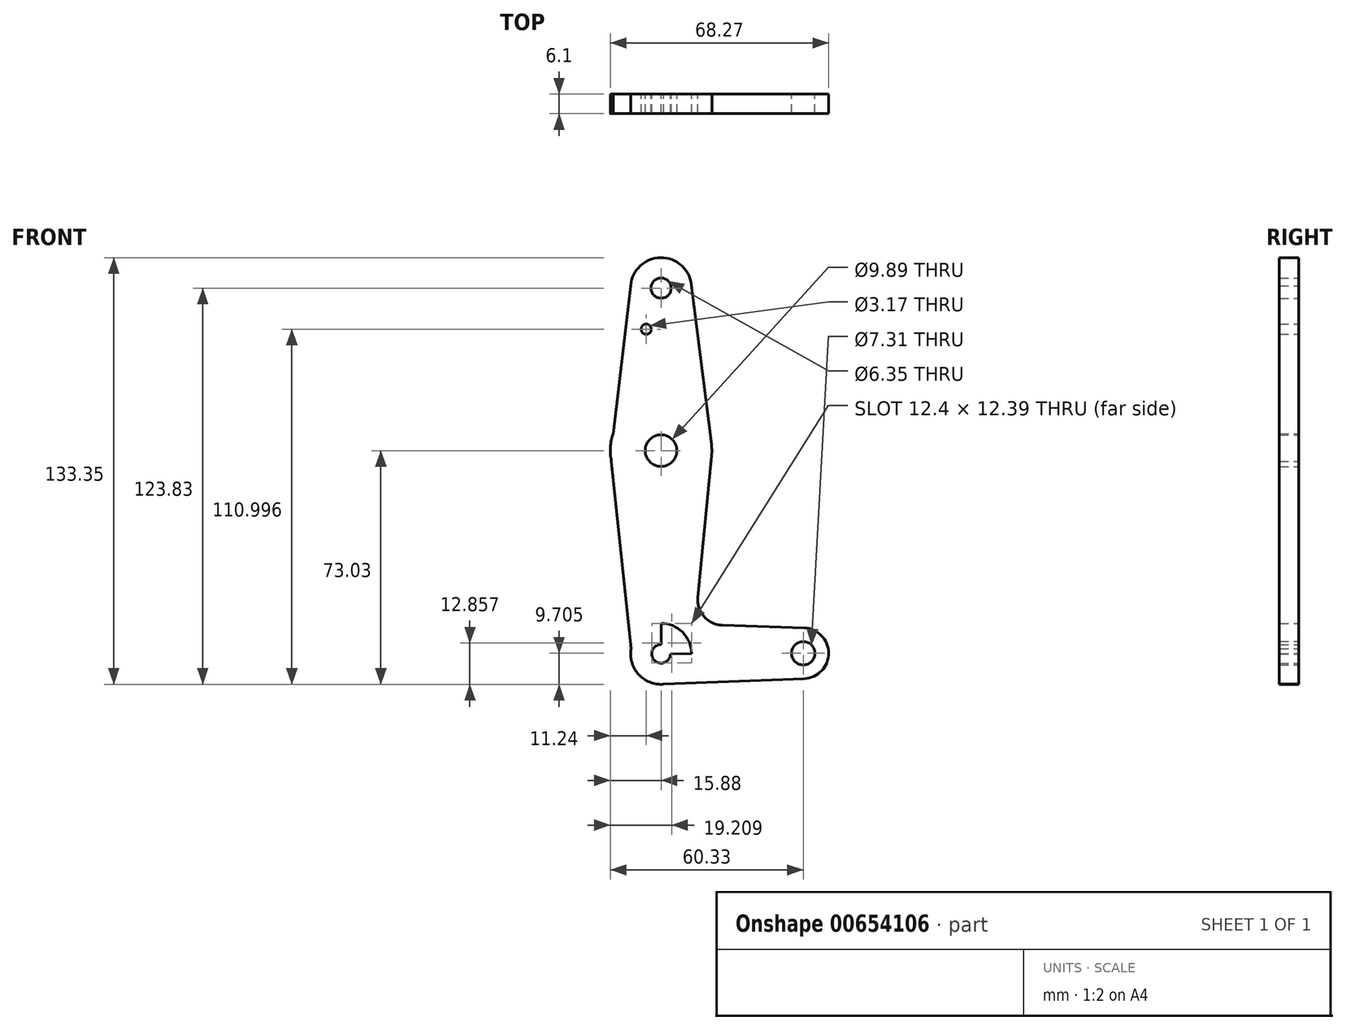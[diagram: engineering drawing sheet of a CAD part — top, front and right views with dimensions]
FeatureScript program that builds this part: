
annotation { "Feature Type Name" : "Feature", "Feature Type Description" : "" }
export const myFeature = defineFeature(function(context is Context, id is Id, definition is map)
    precondition{}
    {
        {
            var Q0;
            Q0=qCreatedBy(makeId("Front.planeOp"),FACE);
            var sketch = newSketch(context, id + "F0", { "sketchPlane" : qUnion([Q0])});
            skCircle(sketch, "E0", {"center": v(0, 50.8) * mm, "radius": 9.53 * mm});
            skCircle(sketch, "E1", {"center": v(0, 0) * mm, "radius": 15.88 * mm});
            skCircle(sketch, "E2", {"center": v(0, -63.5) * mm, "radius": 9.53 * mm});
            skCircle(sketch, "E3", {"center": v(44.45, -63.33) * mm, "radius": 7.94 * mm});
            skLineSegment(sketch, "E4", {"start": v(0, 50.8) * mm, "end": v(0, 0) * mm});
            skLineSegment(sketch, "E5", {"start": v(0, -63.5) * mm, "end": v(44.45, -63.33) * mm});
            skLineSegment(sketch, "E6", {"start": v(0, 0) * mm, "end": v(0, -63.5) * mm});
            skLineSegment(sketch, "E7", {"start": v(0, 50.8) * mm, "end": v(0, -63.5) * mm});
            skLineSegment(sketch, "E8", {"start": v(-9.41, 52.27) * mm, "end": v(-14.96, 5.32) * mm});
            skLineSegment(sketch, "E9", {"start": v(9.45, 52.03) * mm, "end": v(15.75, 1.98) * mm});
            skLineSegment(sketch, "E10", {"start": v(15.8, -1.53) * mm, "end": v(11.52, -45.87) * mm});
            skLineSegment(sketch, "E11", {"start": v(-15.88, 0) * mm, "end": v(-9.38, -61.83) * mm});
            skLineSegment(sketch, "E12", {"start": v(19.18, -54.58) * mm, "end": v(44.7, -55.4) * mm});
            skLineSegment(sketch, "E13", {"start": v(0, -73.03) * mm, "end": v(44.76, -71.26) * mm});
            skPoint(sketch, "E13.startSnap0", {"position": v(0, -31.75) * mm});
            skArc(sketch, "E14.filletArc", {"start": v(11.52, -45.87) * mm, "mid": v(13.46, -51.89) * mm, "end": v(19.18, -54.58) * mm});
            skCircle(sketch, "E15", {"center": v(-4.64, 37.97) * mm, "radius": 1.59 * mm});
            skCircle(sketch, "E16", {"center": v(0, 50.8) * mm, "radius": 3.18 * mm});
            skCircle(sketch, "E17", {"center": v(0, 0) * mm, "radius": 4.95 * mm});
            skCircle(sketch, "E18", {"center": v(0, -63.5) * mm, "radius": 2.92 * mm});
            skCircle(sketch, "E19", {"center": v(44.45, -63.33) * mm, "radius": 3.66 * mm});
            skSolve(sketch);
        }
        {
            var Q0;
            Q0 = qSketchRegion(id + "F0", true);
            extrude(context, id + "F1", {"entities" : qUnion([Q0]), "depth" : 3.05 * mm, "offsetDistance" : 25.4 * mm});
        }
        {
            var Q0;
            Q0 = qSketchRegion(id + "F0", true);
            var Q1;
            Q1=makeQuery(id+"F1.opExtrude","CAP_FACE",FACE,{"disambiguationData":[OSD([sQuery(id+"F0.wireOp",EDGE,"E0"),sQuery(id+"F0.wireOp",EDGE,"E1"),sQuery(id+"F0.wireOp",EDGE,"E2"),sQuery(id+"F0.wireOp",EDGE,"E3"),sQuery(id+"F0.wireOp",EDGE,"E5"),sQuery(id+"F0.wireOp",EDGE,"E7"),sQuery(id+"F0.wireOp",EDGE,"E8"),sQuery(id+"F0.wireOp",EDGE,"E9"),sQuery(id+"F0.wireOp",EDGE,"E10"),sQuery(id+"F0.wireOp",EDGE,"E11"),sQuery(id+"F0.wireOp",EDGE,"E12"),sQuery(id+"F0.wireOp",EDGE,"E13"),sQuery(id+"F0.wireOp",EDGE,"E14.filletArc"),sQuery(id+"F0.wireOp",EDGE,"E15"),sQuery(id+"F0.wireOp",EDGE,"E16"),sQuery(id+"F0.wireOp",EDGE,"E17"),sQuery(id+"F0.wireOp",EDGE,"E18"),sQuery(id+"F0.wireOp",EDGE,"E19")])],"isStart":false});
            extrude(context, id + "F2", {"entities" : qUnion([Q0, Q1]), "operationType" : NewBodyOperationType.ADD, "depth" : 3.05 * mm, "offsetDistance" : 25.4 * mm});
        }
    });
